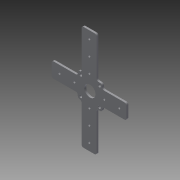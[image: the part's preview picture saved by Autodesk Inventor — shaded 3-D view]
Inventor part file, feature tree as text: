
AUTODESK INVENTOR PART (.ipt)
format: ipt  version: 2014 (Build 180170000, 170)  size: 176,640 bytes
history: native  units: in
note: dims shown in document units (in); Inventor stores cm internally (conversion verified against a paired STEP export)
features: extrude x1, fillet x1, sketch x1
ambient origin geometry x8: Origin, YZ Plane, XZ Plane, XY Plane, X Axis, Y Axis, Z Axis, Center Point
bodies: Solid1 (feature_tree)
feature tree (3):
  extrude  "Extrusion1"  Depth=0.125in
  fillet  "Fillet1"  Radius=1.0in
  sketch  "Sketch1"  dims[d1=0.7874in d3=0.7874in d5=1.1811in d7=0.3937in d9=1.1811in d11=0.3937in d12=1.0in d13=5.0in d14=1.625in d15=0.164in d16=0.164in d17=1.25in d18=1.25in d19=0.1875in d20=0.5in d21=0.5in d22=0.5in d23=0.188in d24=1.25in d25=1.25in d26=0.75in d27=0.8125in d28=2.44in d29=0.5in d30=1.0in d31=2.0in d32=3.0in d33=1.0in d34=3.0in d35=1.625in d36=0.1875in d37=0.8125in d38=0.164in d39=0.164in d40=0.5in d41=0.5in d42=1.0in d43=0.5in d44=0.5in d45=1.0in d46=1.0in d47=1.0in d48=0.125in d49=0.0in d50=0.125in d51=0.7874in d53=1.0in d54=0.3937in d56=1.0in d58=0.7874in d60=1.0in d61=0.3937in d63=1.0in]
